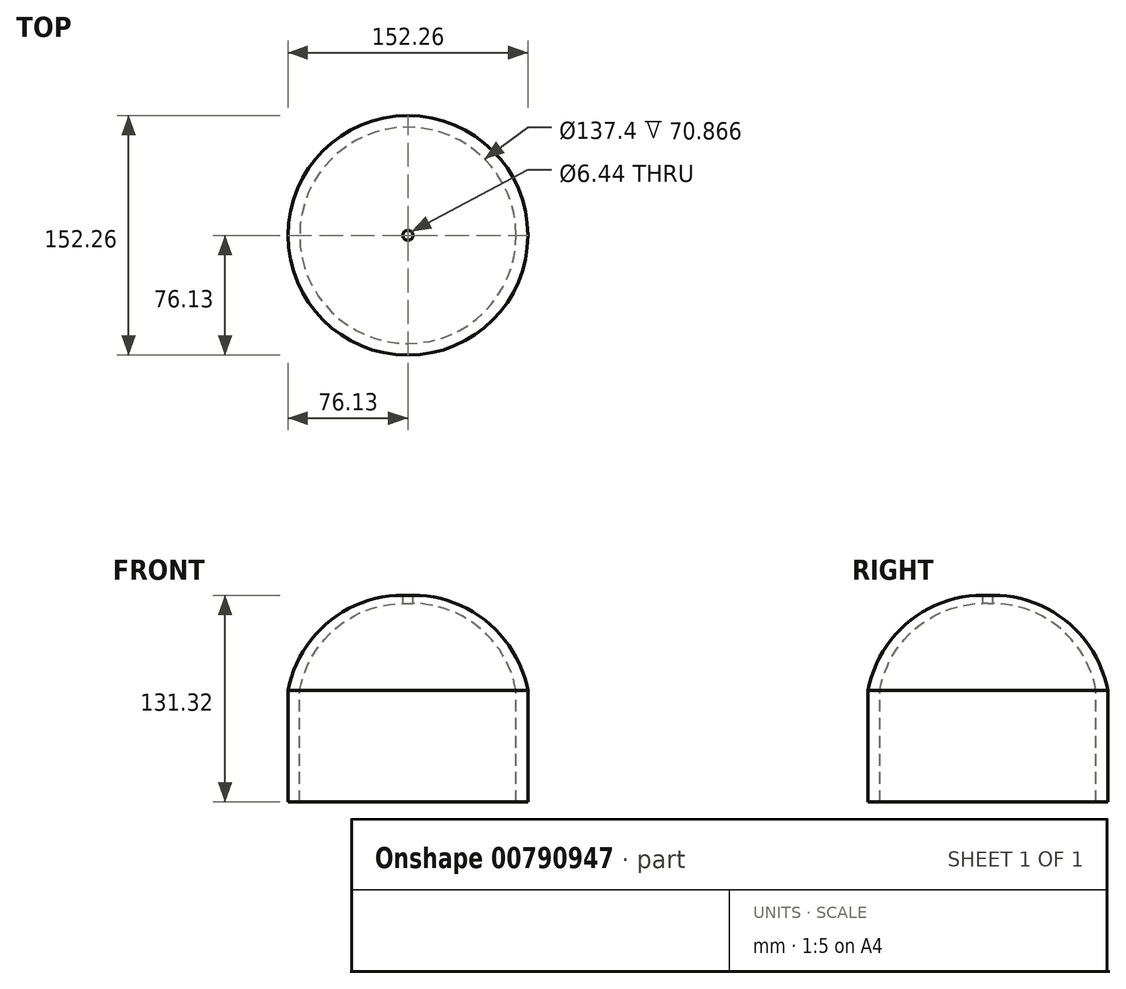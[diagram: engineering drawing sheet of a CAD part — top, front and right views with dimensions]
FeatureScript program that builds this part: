
annotation { "Feature Type Name" : "Feature", "Feature Type Description" : "" }
export const myFeature = defineFeature(function(context is Context, id is Id, definition is map)
    precondition{}
    {
        {
            var Q0;
            Q0=qCreatedBy(makeId("Top.planeOp"),FACE);
            var sketch = newSketch(context, id + "F0", { "sketchPlane" : qUnion([Q0])});
            skCircle(sketch, "E0", {"center": v(0, 0) * mm, "radius": 76.13 * mm});
            skSolve(sketch);
        }
        {
            var Q0;
            Q0 = qSketchRegion(id + "F0", true);
            extrude(context, id + "F1", {"entities" : qUnion([Q0]), "depth" : 60.45 * mm, "offsetDistance" : 25.4 * mm});
        }
        {
            var Q0;
            Q0=makeQuery(id+"F1.opExtrude","CAP_FACE",FACE,{"disambiguationData":[OSD([sQuery(id+"F0.wireOp",EDGE,"E0")])],"isStart":true});
            var sketch = newSketch(context, id + "F2", { "sketchPlane" : qUnion([Q0])});
            skCircle(sketch, "E1", {"center": v(0, 0) * mm, "radius": 68.7 * mm});
            skSolve(sketch);
        }
        {
            var Q0;
            Q0 = qSketchRegion(id + "F2", true);
            extrude(context, id + "F3", {"entities" : qUnion([Q0]), "operationType" : NewBodyOperationType.REMOVE, "oppositeDirection" : true, "depth" : 55.37 * mm, "offsetDistance" : 25.4 * mm});
        }
        {
            var Q0;
            Q0=makeQuery(id+"F3.boolean.opBoolean","COPY",EDGE,{"derivedFrom":makeQuery(id+"F3.opExtrude","CAP_EDGE",EDGE,{"disambiguationData":[OSD([sQuery(id+"F2.wireOp",EDGE,"E1")])],"isStart":false})});
            fillet(context, id + "F4", {"entities" : qUnion([Q0]), "radius" : 67.45 * mm, "tangentPropagation" : true, "allowEdgeOverflow" : false});
        }
        {
            var Q0;
            Q0=makeQuery(id+"F1.opExtrude","CAP_EDGE",EDGE,{"disambiguationData":[OSD([sQuery(id+"F0.wireOp",EDGE,"E0")])],"isStart":false});
            fillet(context, id + "F5", {"entities" : qUnion([Q0]), "radius" : 74.2 * mm, "tangentPropagation" : true, "allowEdgeOverflow" : false});
        }
        {
            var Q0;
            Q0=makeQuery(id+"F1.opExtrude","CAP_FACE",FACE,{"disambiguationData":[OSD([sQuery(id+"F0.wireOp",EDGE,"E0")])],"isStart":true});
            extrude(context, id + "F6", {"entities" : qUnion([Q0]), "operationType" : NewBodyOperationType.ADD, "depth" : 70.87 * mm, "offsetDistance" : 25.4 * mm});
        }
        {
            var Q0;
            Q0=makeQuery(id+"F1.opExtrude","CAP_FACE",FACE,{"disambiguationData":[OSD([sQuery(id+"F0.wireOp",EDGE,"E0")])],"isStart":false});
            extrude(context, id + "F7", {"entities" : qUnion([Q0]), "operationType" : NewBodyOperationType.REMOVE, "oppositeDirection" : true, "depth" : 25.4 * mm, "offsetDistance" : 25.4 * mm});
        }
    });
